# Revit family: Hand_Dryer-Excel_Dryer-ThinAir
name_source: partatom
category: Specialty Equipment
revit_build: Autodesk Revit 2015 (Build: 20140606_1530(x64)
units: mm (PartAtom-declared; Revit-internal decimal feet)

## types (3) — shared parameters
Air Temperature (Farenheit) = 141 °F
Assembly Code = C1030200
Category = Toilet Accessories
Cover Finish = ABS -  Excel Dryer  - White
Default Elevation = 3' - 3"
Depth = 0' - 4"
Description = ThinAir Series
Heating Element = 500 W
Height = 1' - 1 15/16"
Impact Resistant Note = UL 499
Manufacturer = Excel Dryer
Manufacturer Fax = 1-413-525-2853
Manufacturer Toll Free Number = 800-255-9235
Number of Poles = 1
Output at Outlet (LFM) = 16000 LFM
Phase = 1
Power Factor = 1
Product Name = ThinAir Excel Dryer®
Product Page URL = http://www.exceldryer.com
Product Weight = 8 lbs
Product data url = https://bimobject.com
Subcategory = Hand Dryers
URL = http://www.exceldryer.com
Warranty Duration = 5 Years
Width = 0' - 8 29/32"

## per-type parameters (varying)
| type | Amperage | Apparent Load | Frequency | Voltage | Watts |
| TA-ABS-110-120V 7-7.7A - 770-915W | 8 A | 960 VA | 60 Hz | 120 V | 915 W |
| TA-ABS-208-277V 3.6-4A - 735-950W | 4 A | 984 VA | 60 Hz | 277 V | 950 W |
| TA-ABS-230V 3.9A 890W | 4 A | 920 VA | 50 Hz | 230 V | 890 W |

note: column(s) folded — value = type name in every type: Model

## geometry (parser evidence)
native form markers: Blend x18, Sweep x2
no freeform markers — native parametric forms only
